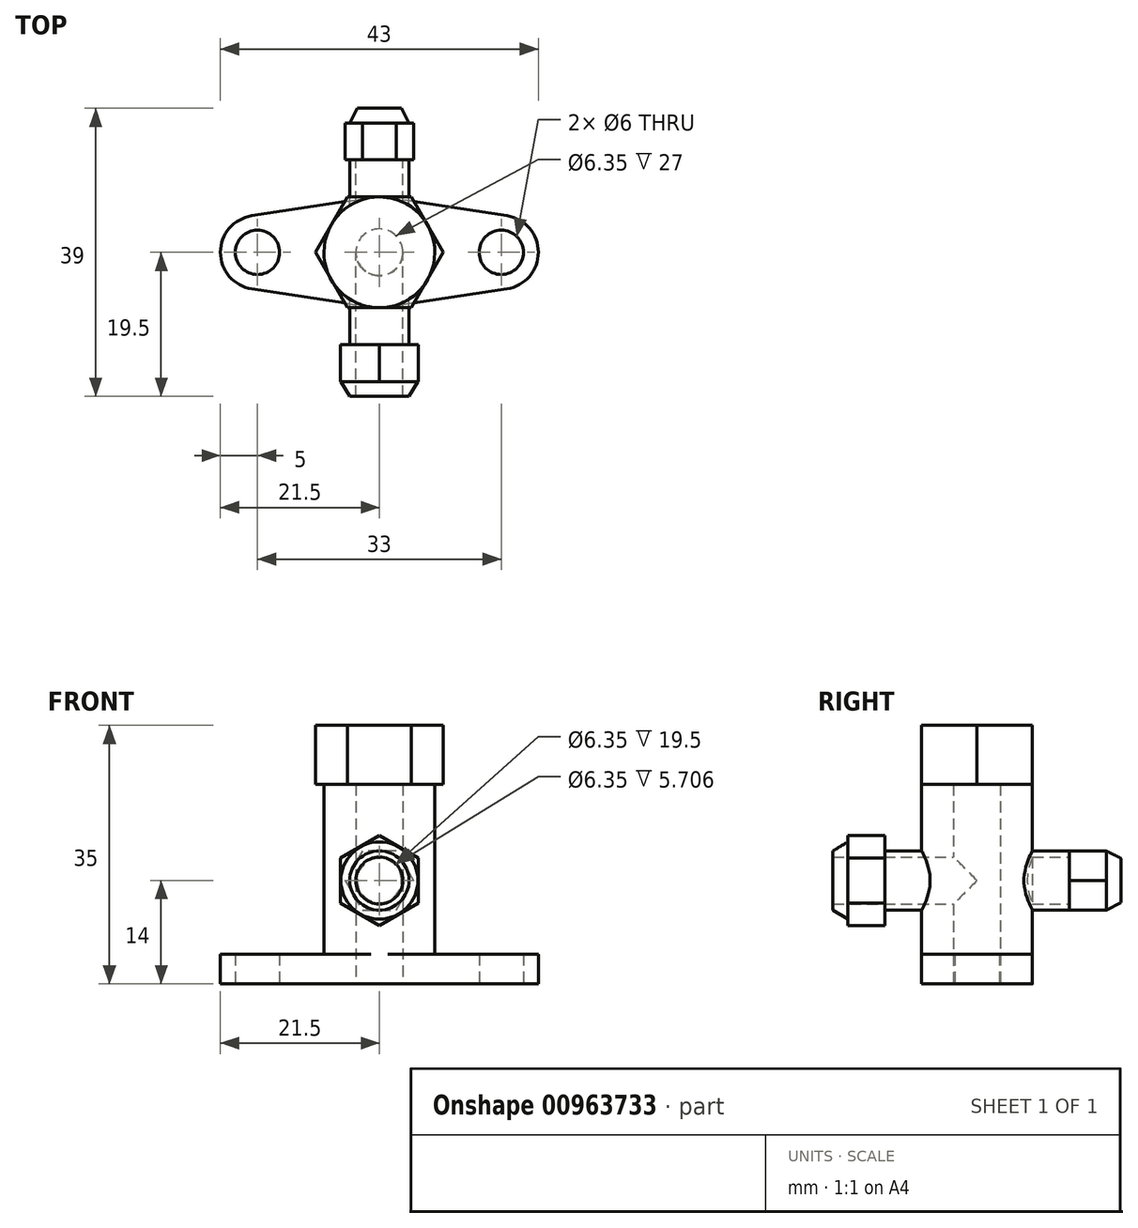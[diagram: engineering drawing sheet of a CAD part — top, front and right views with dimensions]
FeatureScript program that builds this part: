
annotation { "Feature Type Name" : "Feature", "Feature Type Description" : "" }
export const myFeature = defineFeature(function(context is Context, id is Id, definition is map)
    precondition{}
    {
        {
            var Q0;
            Q0=qCreatedBy(makeId("Top.planeOp"),FACE);
            var sketch = newSketch(context, id + "F0", { "sketchPlane" : qUnion([Q0])});
            skCircle(sketch, "E0", {"center": v(0, 0) * mm, "radius": 7.5 * mm});
            skLineSegment(sketch, "E1", {"start": v(0, 0) * mm, "end": v(16.5, 0) * mm, "construction": true});
            skLineSegment(sketch, "E2", {"start": v(0, 0) * mm, "end": v(-16.5, 0) * mm, "construction": true});
            skArc(sketch, "E3", {"start": v(-17.26, 4.94) * mm, "mid": v(-21.5, 0) * mm, "end": v(-17.26, -4.94) * mm});
            skArc(sketch, "E4", {"start": v(17.26, -4.94) * mm, "mid": v(21.5, 0) * mm, "end": v(17.26, 4.94) * mm});
            skLineSegment(sketch, "E5", {"start": v(17.26, 4.94) * mm, "end": v(1.14, 7.41) * mm});
            skLineSegment(sketch, "E6", {"start": v(-17.26, 4.94) * mm, "end": v(-1.14, 7.41) * mm});
            skLineSegment(sketch, "E7", {"start": v(-17.26, -4.94) * mm, "end": v(-1.14, -7.41) * mm});
            skLineSegment(sketch, "E8", {"start": v(17.26, -4.94) * mm, "end": v(1.14, -7.41) * mm});
            skCircle(sketch, "E9", {"center": v(-16.5, 0) * mm, "radius": 3 * mm});
            skCircle(sketch, "E10", {"center": v(16.5, 0) * mm, "radius": 3 * mm});
            skCircle(sketch, "E11", {"center": v(0, 0) * mm, "radius": 3.18 * mm});
            skSolve(sketch);
        }
        {
            var Q0;
            Q0=makeQuery(id+"F0.imprint","IMPRINT",FACE,{"disambiguationData":[TD([[makeQuery(id+"F0.imprint","IMPRINT",EDGE,{"derivedFrom":sQuery(id+"F0.wireOp",EDGE,"E3")}),1.0]])]});
            var Q1;
            Q1=makeQuery(id+"F0.imprint","IMPRINT",FACE,{"disambiguationData":[TD([[makeQuery(id+"F0.imprint","IMPRINT",EDGE,{"derivedFrom":sQuery(id+"F0.wireOp",EDGE,"E4")}),1.0]])]});
            extrude(context, id + "F1", {"entities" : qUnion([Q0, Q1]), "depth" : 4 * mm, "offsetDistance" : 25 * mm});
        }
        {
            var Q0;
            Q0=makeQuery(id+"F0.imprint","IMPRINT",FACE,{"disambiguationData":[TD([[makeQuery(id+"F0.imprint","IMPRINT",EDGE,{"derivedFrom":sQuery(id+"F0.wireOp",EDGE,"E11")}),-1.0]])]});
            extrude(context, id + "F2", {"entities" : qUnion([Q0]), "operationType" : NewBodyOperationType.ADD, "depth" : 27 * mm, "offsetDistance" : 25 * mm});
        }
        {
            var Q0;
            Q0=makeQuery(id+"F2.opExtrude","CAP_FACE",FACE,{"disambiguationData":[OSD([sQuery(id+"F0.wireOp",EDGE,"E0"),sQuery(id+"F0.wireOp",EDGE,"E11")])],"isStart":false});
            var sketch = newSketch(context, id + "F3", { "sketchPlane" : qUnion([Q0])});
            skCircle(sketch, "E12.cCircle", {"center": v(0, 0) * mm, "radius": 7.5 * mm, "construction": true});
            skLineSegment(sketch, "E12.0", {"start": v(4.33, -7.5) * mm, "end": v(-4.33, -7.5) * mm});
            skLineSegment(sketch, "E12.1", {"start": v(-4.33, -7.5) * mm, "end": v(-8.66, 0) * mm});
            skLineSegment(sketch, "E12.2", {"start": v(-8.66, 0) * mm, "end": v(-4.33, 7.5) * mm});
            skLineSegment(sketch, "E12.3", {"start": v(-4.33, 7.5) * mm, "end": v(4.33, 7.5) * mm});
            skLineSegment(sketch, "E12.4", {"start": v(4.33, 7.5) * mm, "end": v(8.66, 0) * mm});
            skLineSegment(sketch, "E12.5", {"start": v(8.66, 0) * mm, "end": v(4.33, -7.5) * mm});
            skPoint(sketch, "E12.0.midPoint", {"position": v(0, -7.5) * mm});
            skSolve(sketch);
        }
        {
            var Q0;
            Q0=makeQuery(id+"F3.imprint","IMPRINT",FACE,{"disambiguationData":[TD([[makeQuery(id+"F3.imprint","IMPRINT",EDGE,{"derivedFrom":makeQuery(id+"F2.opExtrude","CAP_EDGE",EDGE,{"disambiguationData":[OSD([sQuery(id+"F0.wireOp",EDGE,"E11")])],"isStart":false})}),-1.0]])]});
            var Q1;
            {var subQ0=sQuery(id+"F3.wireOp",EDGE,"E12.1");var subQ1=sQuery(id+"F3.wireOp",EDGE,"E12.0");var subQ2=makeQuery(id+"F3.imprint","INTERSECT",VERTEX,{"derivedFrom":[subQ1,subQ0]});Q1=makeQuery(id+"F3.imprint","IMPRINT",FACE,{"disambiguationData":[TD([[makeQuery(id+"F3.imprint","IMPRINT",EDGE,{"disambiguationData":[TD([[subQ2,1.0]])],"derivedFrom":subQ1}),-1.0]])]});}
            var Q2;
            {var subQ0=sQuery(id+"F3.wireOp",EDGE,"E12.2");var subQ1=sQuery(id+"F3.wireOp",EDGE,"E12.1");var subQ2=makeQuery(id+"F3.imprint","INTERSECT",VERTEX,{"derivedFrom":[subQ1,subQ0]});Q2=makeQuery(id+"F3.imprint","IMPRINT",FACE,{"disambiguationData":[TD([[makeQuery(id+"F3.imprint","IMPRINT",EDGE,{"disambiguationData":[TD([[subQ2,1.0]])],"derivedFrom":subQ1}),-1.0]])]});}
            var Q3;
            {var subQ0=sQuery(id+"F3.wireOp",EDGE,"E12.5");var subQ1=sQuery(id+"F3.wireOp",EDGE,"E12.0");var subQ2=makeQuery(id+"F3.imprint","INTERSECT",VERTEX,{"derivedFrom":[subQ1,subQ0]});Q3=makeQuery(id+"F3.imprint","IMPRINT",FACE,{"disambiguationData":[TD([[makeQuery(id+"F3.imprint","IMPRINT",EDGE,{"disambiguationData":[TD([[subQ2,-1.0]])],"derivedFrom":subQ1}),-1.0]])]});}
            var Q4;
            {var subQ0=sQuery(id+"F3.wireOp",EDGE,"E12.5");var subQ1=sQuery(id+"F3.wireOp",EDGE,"E12.4");var subQ2=makeQuery(id+"F3.imprint","INTERSECT",VERTEX,{"derivedFrom":[subQ1,subQ0]});Q4=makeQuery(id+"F3.imprint","IMPRINT",FACE,{"disambiguationData":[TD([[makeQuery(id+"F3.imprint","IMPRINT",EDGE,{"disambiguationData":[TD([[subQ2,1.0]])],"derivedFrom":subQ1}),-1.0]])]});}
            var Q5;
            {var subQ0=sQuery(id+"F3.wireOp",EDGE,"E12.4");var subQ1=sQuery(id+"F3.wireOp",EDGE,"E12.3");var subQ2=makeQuery(id+"F3.imprint","INTERSECT",VERTEX,{"derivedFrom":[subQ1,subQ0]});Q5=makeQuery(id+"F3.imprint","IMPRINT",FACE,{"disambiguationData":[TD([[makeQuery(id+"F3.imprint","IMPRINT",EDGE,{"disambiguationData":[TD([[subQ2,1.0]])],"derivedFrom":subQ1}),-1.0]])]});}
            var Q6;
            {var subQ0=sQuery(id+"F3.wireOp",EDGE,"E12.3");var subQ1=sQuery(id+"F3.wireOp",EDGE,"E12.2");var subQ2=makeQuery(id+"F3.imprint","INTERSECT",VERTEX,{"derivedFrom":[subQ1,subQ0]});Q6=makeQuery(id+"F3.imprint","IMPRINT",FACE,{"disambiguationData":[TD([[makeQuery(id+"F3.imprint","IMPRINT",EDGE,{"disambiguationData":[TD([[subQ2,1.0]])],"derivedFrom":subQ1}),-1.0]])]});}
            extrude(context, id + "F4", {"entities" : qUnion([Q0, Q1, Q2, Q3, Q4, Q5, Q6]), "operationType" : NewBodyOperationType.ADD, "depth" : 8 * mm, "offsetDistance" : 25 * mm});
        }
        {
            var Q0;
            Q0=makeQuery(id+"F4.opExtrude","CAP_FACE",FACE,{"disambiguationData":[OSD([sQuery(id+"F0.wireOp",EDGE,"E11"),sQuery(id+"F3.wireOp",EDGE,"E12.0"),sQuery(id+"F3.wireOp",EDGE,"E12.1"),sQuery(id+"F3.wireOp",EDGE,"E12.2"),sQuery(id+"F3.wireOp",EDGE,"E12.3"),sQuery(id+"F3.wireOp",EDGE,"E12.4"),sQuery(id+"F3.wireOp",EDGE,"E12.5")])],"isStart":false});
            var sketch = newSketch(context, id + "F5", { "sketchPlane" : qUnion([Q0])});
            skCircle(sketch, "E13", {"center": v(0, 0) * mm, "radius": 3.14 * mm});
            skSolve(sketch);
        }
        {
            var Q0;
            Q0=makeQuery(id+"F5.imprint","IMPRINT",FACE,{"disambiguationData":[TD([[makeQuery(id+"F5.imprint","IMPRINT",EDGE,{"derivedFrom":makeQuery(id+"F4.opExtrude","CAP_EDGE",EDGE,{"disambiguationData":[OSD([sQuery(id+"F3.wireOp",EDGE,"E12.0")])],"isStart":false})}),-1.0]])]});
            var sketch = newSketch(context, id + "F6", { "sketchPlane" : qUnion([Q0])});
            skCircle(sketch, "E14", {"center": v(0, 0) * mm, "radius": 5.72 * mm});
            skSolve(sketch);
        }
        {
            var Q0;
            Q0=makeQuery(id+"F6.imprint","IMPRINT",FACE,{"disambiguationData":[TD([[makeQuery(id+"F6.imprint","IMPRINT",EDGE,{"derivedFrom":sQuery(id+"F6.wireOp",EDGE,"E14")}),1.0]])]});
            var Q1;
            Q1=makeQuery(id+"F6.imprint","IMPRINT",FACE,{"disambiguationData":[TD([[makeQuery(id+"F6.imprint","IMPRINT",EDGE,{"derivedFrom":makeQuery(id+"F5.imprint","IMPRINT",EDGE,{"derivedFrom":makeQuery(id+"F4.opExtrude","CAP_EDGE",EDGE,{"disambiguationData":[OSD([sQuery(id+"F0.wireOp",EDGE,"E11")])],"isStart":false})})}),1.0]])]});
            extrude(context, id + "F7", {"entities" : qUnion([Q0, Q1]), "operationType" : NewBodyOperationType.ADD, "oppositeDirection" : true, "depth" : 8 * mm, "offsetDistance" : 25 * mm});
        }
        {
            var Q0;
            Q0=qCreatedBy(makeId("Front.planeOp"),FACE);
            var sketch = newSketch(context, id + "F8", { "sketchPlane" : qUnion([Q0])});
            skLineSegment(sketch, "E15", {"start": v(0, 0) * mm, "end": v(0, 14) * mm});
            skCircle(sketch, "E16", {"center": v(0, 14) * mm, "radius": 3.18 * mm});
            skCircle(sketch, "E17", {"center": v(0, 14) * mm, "radius": 4 * mm});
            skSolve(sketch);
        }
        {
            var Q0;
            Q0=makeQuery(id+"F8.imprint","IMPRINT",FACE,{"disambiguationData":[TD([[makeQuery(id+"F8.imprint","IMPRINT",EDGE,{"derivedFrom":sQuery(id+"F8.wireOp",EDGE,"E16")}),-1.0]])]});
            extrude(context, id + "F9", {"entities" : qUnion([Q0]), "operationType" : NewBodyOperationType.ADD, "endBound" : BoundingType.SYMMETRIC, "depth" : 35 * mm, "offsetDistance" : 25 * mm});
        }
        {
            var Q0;
            Q0=makeQuery(id+"F0.imprint","IMPRINT",FACE,{"disambiguationData":[TD([[makeQuery(id+"F0.imprint","IMPRINT",EDGE,{"derivedFrom":sQuery(id+"F0.wireOp",EDGE,"E11")}),1.0]])]});
            extrude(context, id + "F10", {"entities" : qUnion([Q0]), "operationType" : NewBodyOperationType.REMOVE, "depth" : 18 * mm, "offsetDistance" : 25 * mm});
        }
        {
            var Q0;
            Q0=makeQuery(id+"F9.opExtrude","CAP_FACE",FACE,{"disambiguationData":[OSD([sQuery(id+"F8.wireOp",EDGE,"E16"),sQuery(id+"F8.wireOp",EDGE,"E17")])],"isStart":false});
            var sketch = newSketch(context, id + "F11", { "sketchPlane" : qUnion([Q0])});
            skCircle(sketch, "E18.cCircle", {"center": v(0, 14) * mm, "radius": 5.3 * mm, "construction": true});
            skLineSegment(sketch, "E18.0", {"start": v(5.3, 17.05) * mm, "end": v(5.3, 10.95) * mm});
            skLineSegment(sketch, "E18.1", {"start": v(5.3, 10.95) * mm, "end": v(0, 7.9) * mm});
            skLineSegment(sketch, "E18.2", {"start": v(0, 7.9) * mm, "end": v(-5.3, 10.95) * mm});
            skLineSegment(sketch, "E18.3", {"start": v(-5.3, 10.95) * mm, "end": v(-5.3, 17.05) * mm});
            skLineSegment(sketch, "E18.4", {"start": v(-5.3, 17.05) * mm, "end": v(0, 20.1) * mm});
            skLineSegment(sketch, "E18.5", {"start": v(0, 20.1) * mm, "end": v(5.3, 17.05) * mm});
            skPoint(sketch, "E18.0.midPoint", {"position": v(5.3, 14) * mm});
            skSolve(sketch);
        }
        {
            var Q0;
            Q0=makeQuery(id+"F11.imprint","IMPRINT",FACE,{"disambiguationData":[TD([[makeQuery(id+"F11.imprint","IMPRINT",EDGE,{"derivedFrom":sQuery(id+"F11.wireOp",EDGE,"E18.0")}),-1.0]])]});
            var Q1;
            Q1=makeQuery(id+"F11.imprint","IMPRINT",FACE,{"disambiguationData":[TD([[makeQuery(id+"F11.imprint","IMPRINT",EDGE,{"derivedFrom":makeQuery(id+"F9.opExtrude","CAP_EDGE",EDGE,{"disambiguationData":[OSD([sQuery(id+"F8.wireOp",EDGE,"E16")])],"isStart":false})}),1.0]])]});
            extrude(context, id + "F12", {"entities" : qUnion([Q0, Q1]), "operationType" : NewBodyOperationType.ADD, "oppositeDirection" : true, "depth" : 5 * mm, "offsetDistance" : 25 * mm});
        }
        {
            var Q0;
            Q0=makeQuery(id+"F9.opExtrude","CAP_FACE",FACE,{"disambiguationData":[OSD([sQuery(id+"F8.wireOp",EDGE,"E16"),sQuery(id+"F8.wireOp",EDGE,"E17")])],"isStart":true});
            var sketch = newSketch(context, id + "F13", { "sketchPlane" : qUnion([Q0])});
            skCircle(sketch, "E19.cCircle", {"center": v(0, 14) * mm, "radius": 4 * mm, "construction": true});
            skLineSegment(sketch, "E19.0", {"start": v(2.3, 10) * mm, "end": v(-2.3, 10) * mm});
            skLineSegment(sketch, "E19.1", {"start": v(-2.3, 10) * mm, "end": v(-4.62, 14) * mm});
            skLineSegment(sketch, "E19.2", {"start": v(-4.62, 14) * mm, "end": v(-2.3, 18) * mm});
            skLineSegment(sketch, "E19.3", {"start": v(-2.3, 18) * mm, "end": v(2.3, 18) * mm});
            skLineSegment(sketch, "E19.4", {"start": v(2.3, 18) * mm, "end": v(4.62, 14) * mm});
            skLineSegment(sketch, "E19.5", {"start": v(4.62, 14) * mm, "end": v(2.3, 10) * mm});
            skPoint(sketch, "E19.0.midPoint", {"position": v(0, 10) * mm});
            skSolve(sketch);
        }
        {
            var Q0;
            Q0=makeQuery(id+"F13.imprint","IMPRINT",FACE,{"disambiguationData":[TD([[makeQuery(id+"F13.imprint","IMPRINT",EDGE,{"derivedFrom":makeQuery(id+"F9.opExtrude","CAP_EDGE",EDGE,{"disambiguationData":[OSD([sQuery(id+"F8.wireOp",EDGE,"E16")])],"isStart":true})}),1.0]])]});
            var Q1;
            {var subQ0=sQuery(id+"F13.wireOp",EDGE,"E19.5");var subQ1=sQuery(id+"F13.wireOp",EDGE,"E19.4");var subQ2=makeQuery(id+"F13.imprint","INTERSECT",VERTEX,{"derivedFrom":[subQ1,subQ0]});Q1=makeQuery(id+"F13.imprint","IMPRINT",FACE,{"disambiguationData":[TD([[makeQuery(id+"F13.imprint","IMPRINT",EDGE,{"disambiguationData":[TD([[subQ2,1.0]])],"derivedFrom":subQ1}),-1.0]])]});}
            var Q2;
            {var subQ0=sQuery(id+"F13.wireOp",EDGE,"E19.4");var subQ1=sQuery(id+"F13.wireOp",EDGE,"E19.3");var subQ2=makeQuery(id+"F13.imprint","INTERSECT",VERTEX,{"derivedFrom":[subQ1,subQ0]});Q2=makeQuery(id+"F13.imprint","IMPRINT",FACE,{"disambiguationData":[TD([[makeQuery(id+"F13.imprint","IMPRINT",EDGE,{"disambiguationData":[TD([[subQ2,1.0]])],"derivedFrom":subQ1}),-1.0]])]});}
            var Q3;
            {var subQ0=sQuery(id+"F13.wireOp",EDGE,"E19.3");var subQ1=sQuery(id+"F13.wireOp",EDGE,"E19.2");var subQ2=makeQuery(id+"F13.imprint","INTERSECT",VERTEX,{"derivedFrom":[subQ1,subQ0]});Q3=makeQuery(id+"F13.imprint","IMPRINT",FACE,{"disambiguationData":[TD([[makeQuery(id+"F13.imprint","IMPRINT",EDGE,{"disambiguationData":[TD([[subQ2,1.0]])],"derivedFrom":subQ1}),-1.0]])]});}
            var Q4;
            {var subQ0=sQuery(id+"F13.wireOp",EDGE,"E19.2");var subQ1=sQuery(id+"F13.wireOp",EDGE,"E19.1");var subQ2=makeQuery(id+"F13.imprint","INTERSECT",VERTEX,{"derivedFrom":[subQ1,subQ0]});Q4=makeQuery(id+"F13.imprint","IMPRINT",FACE,{"disambiguationData":[TD([[makeQuery(id+"F13.imprint","IMPRINT",EDGE,{"disambiguationData":[TD([[subQ2,1.0]])],"derivedFrom":subQ1}),-1.0]])]});}
            var Q5;
            {var subQ0=sQuery(id+"F13.wireOp",EDGE,"E19.1");var subQ1=sQuery(id+"F13.wireOp",EDGE,"E19.0");var subQ2=makeQuery(id+"F13.imprint","INTERSECT",VERTEX,{"derivedFrom":[subQ1,subQ0]});Q5=makeQuery(id+"F13.imprint","IMPRINT",FACE,{"disambiguationData":[TD([[makeQuery(id+"F13.imprint","IMPRINT",EDGE,{"disambiguationData":[TD([[subQ2,1.0]])],"derivedFrom":subQ1}),-1.0]])]});}
            var Q6;
            {var subQ0=sQuery(id+"F13.wireOp",EDGE,"E19.5");var subQ1=sQuery(id+"F13.wireOp",EDGE,"E19.0");var subQ2=makeQuery(id+"F13.imprint","INTERSECT",VERTEX,{"derivedFrom":[subQ1,subQ0]});Q6=makeQuery(id+"F13.imprint","IMPRINT",FACE,{"disambiguationData":[TD([[makeQuery(id+"F13.imprint","IMPRINT",EDGE,{"disambiguationData":[TD([[subQ2,-1.0]])],"derivedFrom":subQ1}),-1.0]])]});}
            var Q7;
            Q7=makeQuery(id+"F13.imprint","IMPRINT",FACE,{"disambiguationData":[TD([[makeQuery(id+"F13.imprint","IMPRINT",EDGE,{"derivedFrom":makeQuery(id+"F9.opExtrude","CAP_EDGE",EDGE,{"disambiguationData":[OSD([sQuery(id+"F8.wireOp",EDGE,"E16")])],"isStart":true})}),-1.0]])]});
            extrude(context, id + "F14", {"entities" : qUnion([Q0, Q1, Q2, Q3, Q4, Q5, Q6, Q7]), "operationType" : NewBodyOperationType.ADD, "oppositeDirection" : true, "depth" : 5 * mm, "offsetDistance" : 25 * mm});
        }
        {
            var Q0;
            Q0=qCreatedBy(makeId("Right.planeOp"),FACE);
            var sketch = newSketch(context, id + "F15", { "sketchPlane" : qUnion([Q0])});
            skPoint(sketch, "E20.0", {"position": v(0, 14) * mm});
            skLineSegment(sketch, "E21", {"start": v(0, 14) * mm, "end": v(-17.5, 14) * mm});
            skLineSegment(sketch, "E22", {"start": v(0, 14) * mm, "end": v(17.5, 14) * mm});
            skPoint(sketch, "E23.0", {"position": v(-17.5, 20.1) * mm});
            skPoint(sketch, "E24.0", {"position": v(17.5, 18) * mm});
            skLineSegment(sketch, "E25", {"start": v(-17.5, 14) * mm, "end": v(-19.5, 14) * mm});
            skLineSegment(sketch, "E26", {"start": v(-19.5, 14) * mm, "end": v(-19.5, 18) * mm});
            skLineSegment(sketch, "E27", {"start": v(17.5, 14) * mm, "end": v(19.5, 14) * mm});
            skLineSegment(sketch, "E28", {"start": v(19.5, 14) * mm, "end": v(19.5, 17) * mm});
            skLineSegment(sketch, "E29", {"start": v(19.5, 17) * mm, "end": v(17.5, 18) * mm});
            skLineSegment(sketch, "E30", {"start": v(17.5, 18) * mm, "end": v(17.5, 14) * mm});
            skLineSegment(sketch, "E31", {"start": v(-17.5, 14) * mm, "end": v(-17.5, 19.21) * mm});
            skLineSegment(sketch, "E32", {"start": v(-19.5, 18) * mm, "end": v(-17.5, 19.21) * mm});
            skSolve(sketch);
        }
        {
            var Q0;
            Q0=makeQuery(id+"F15.imprint","IMPRINT",FACE,{"disambiguationData":[TD([[makeQuery(id+"F15.imprint","IMPRINT",EDGE,{"derivedFrom":sQuery(id+"F15.wireOp",EDGE,"E27")}),1.0]])]});
            var Q1;
            Q1=makeQuery(id+"F15.imprint","IMPRINT",FACE,{"disambiguationData":[TD([[makeQuery(id+"F15.imprint","IMPRINT",EDGE,{"derivedFrom":sQuery(id+"F15.wireOp",EDGE,"E25")}),-1.0]])]});
            var Q2;
            Q2=sQuery(id+"F15.wireOp",EDGE,"E25");
            revolve(context, id + "F16", {"operationType" : NewBodyOperationType.ADD, "surfaceOperationType" : NewSurfaceOperationType.NEW, "entities" : qUnion([Q0, Q1]), "axis" : qUnion([Q2]), "revolveType" : RevolveType.FULL});
        }
        {
            var Q0;
            Q0=makeQuery(id+"F8.imprint","IMPRINT",FACE,{"disambiguationData":[TD([[makeQuery(id+"F8.imprint","IMPRINT",EDGE,{"derivedFrom":sQuery(id+"F8.wireOp",EDGE,"E16")}),1.0]])]});
            var Q1;
            Q1=makeQuery(id+"F16.opRevolve","SWEPT_FACE",FACE,{"disambiguationData":[OSD([sQuery(id+"F15.wireOp",EDGE,"E26")])]});
            extrude(context, id + "F17", {"entities" : qUnion([Q0]), "operationType" : NewBodyOperationType.REMOVE, "endBound" : BoundingType.UP_TO_SURFACE, "depth" : 35 * mm, "endBoundEntityFace" : qUnion([Q1]), "offsetDistance" : 25 * mm});
        }
    });
